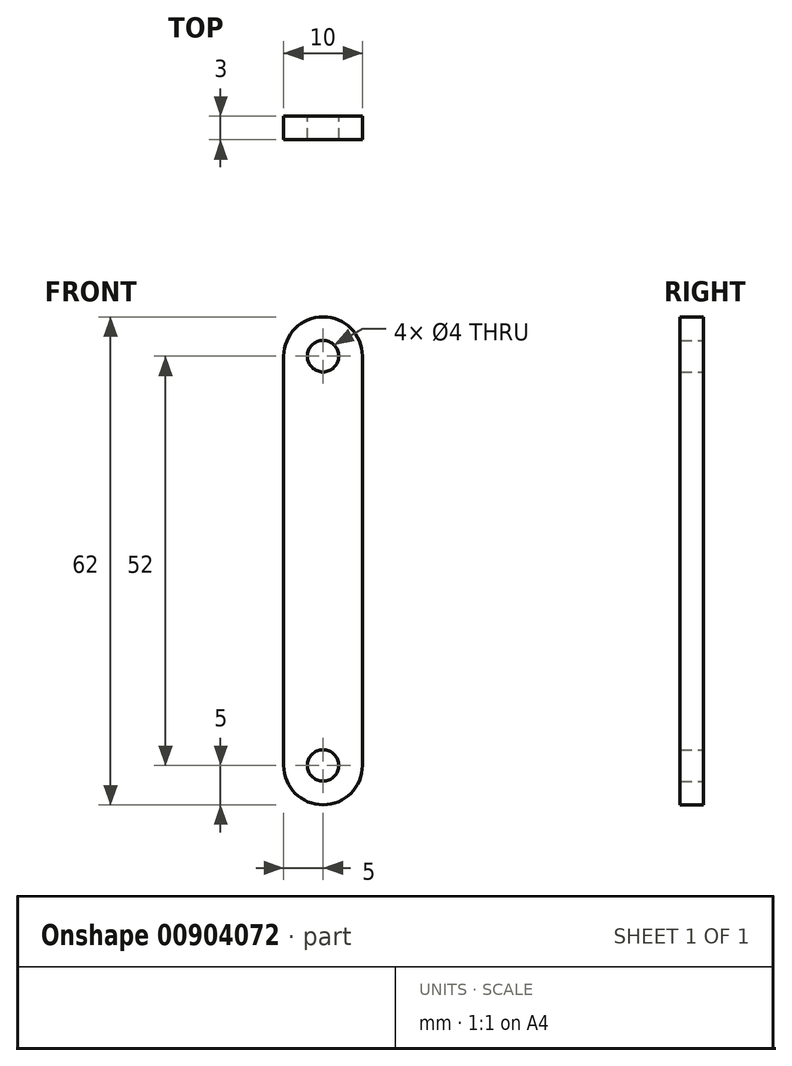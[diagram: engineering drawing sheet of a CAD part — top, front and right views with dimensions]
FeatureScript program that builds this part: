
annotation { "Feature Type Name" : "Feature", "Feature Type Description" : "" }
export const myFeature = defineFeature(function(context is Context, id is Id, definition is map)
    precondition{}
    {
        {
            var Q0;
            Q0=qCreatedBy(makeId("Front.planeOp"),FACE);
            var sketch = newSketch(context, id + "F0", { "sketchPlane" : qUnion([Q0])});
            skArc(sketch, "E0", {"start": v(-5, 0) * mm, "mid": v(0, -5) * mm, "end": v(5, 0) * mm});
            skArc(sketch, "E1", {"start": v(5, 52) * mm, "mid": v(0, 57) * mm, "end": v(-5, 52) * mm});
            skLineSegment(sketch, "E2", {"start": v(-5, 52) * mm, "end": v(-5, 0) * mm});
            skLineSegment(sketch, "E3.MirrorCS", {"start": v(5, 52) * mm, "end": v(5, 0) * mm});
            skCircle(sketch, "E4", {"center": v(0, 52) * mm, "radius": 2 * mm});
            skCircle(sketch, "E5", {"center": v(0, 0) * mm, "radius": 2 * mm});
            skSolve(sketch);
        }
        {
            var Q0;
            Q0 = qSketchRegion(id + "F0", true);
            extrude(context, id + "F1", {"entities" : qUnion([Q0]), "depth" : 3 * mm, "offsetDistance" : 25 * mm});
        }
    });
